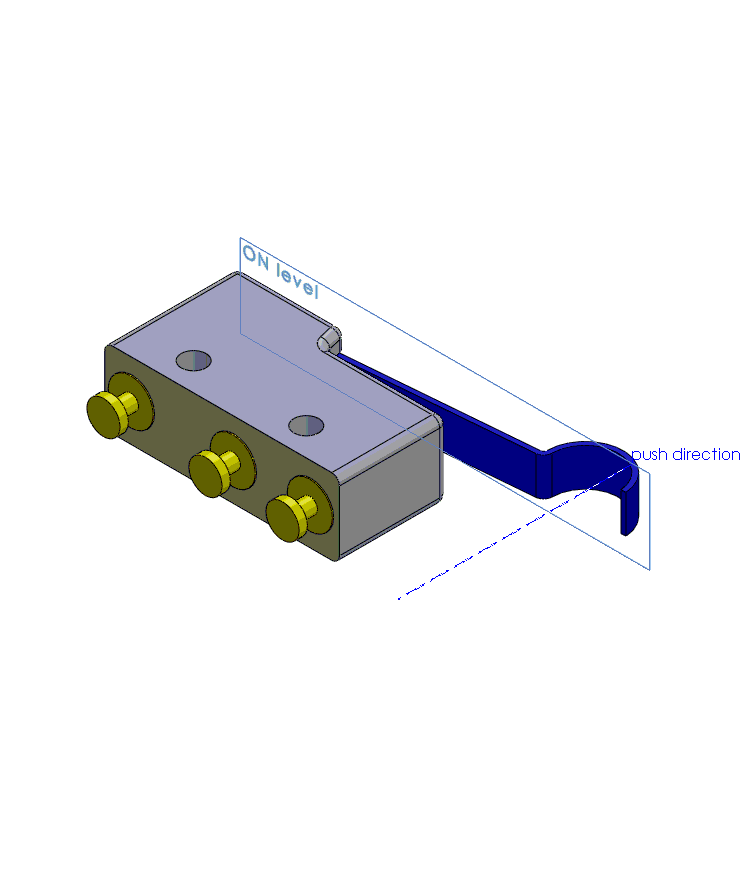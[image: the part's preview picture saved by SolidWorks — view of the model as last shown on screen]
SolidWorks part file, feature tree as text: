
SOLIDWORKS PART (.sldprt)
format: sldprt  version: not decoded by parser v0  size: 303,104 bytes
history: native  units: mm
features: sketch x5, fillet x3, cut_extrude x2, pattern_linear x2, plane x2, material x1, extrude x1, revolve x1 (+11 scaffold rows collapsed)
feature tree (28):
  scaffold x11  (default folders/planes/origin — collapsed)
  material  "Material <not specified>"
  sketch  "Sketch2"  dims[c1.D1=11.2mm c1.D2=19.8mm c2.D1=11.2mm c2.D3=9.0mm c2.D4=9.5mm c2.D5=9.1mm]
  extrude  "Boss-Extrude1"  Depth=6.4mm
  sketch  "Sketch3"  dims[D1=2.1mm D5=2.1mm D2=9.5mm D3=5.15mm D4=5.15mm D6=2.35mm D7=4.1mm D8=1.3mm]
  cut_extrude  "Cut-Extrude1"  Depth=16.4mm
  sketch  "Sketch4"  dims[c1.D1=3.2mm c1.D2=30.22mm c1.D3=~31.402716mm c1.D4=15.5mm c2.D1=3.2mm c2.D5=0.4mm c2.D6=1.0mm c2.D7=5.0mm]
  fillet  "Fillet1"  Radius=0.65mm
  sketch  "Sketch5"
  cut_extrude  "Cut-Extrude2"  Depth=16.4mm
  fillet  "Fillet2"  Radius=0.3mm
  fillet  "Fillet3"  Radius=0.7mm
  sketch  "Sketch6"  dims[D1=1.4mm D2=0.65mm D3=2.4mm D4=0.7mm D5=2.3mm D6=1.9mm D7=0.1mm]
  revolve  "Revolve1"  Angle=360deg
  pattern_linear  "LPattern1"  Count1=2 Count2=1 Spacing1=15.1mm Spacing2=10mm
  pattern_linear  "LPattern2"  Count1=2 Count2=1 Spacing1=8.6mm Spacing2=10mm
  plane  "ON level"  Offset=13mm
  plane  "Plane2"  Offset=28mm
decode coverage: 13 of 14 modeling features carry decoded parameters
note: ~ marks probable driven/reference dimensions
note: suppression state not decoded; provenance and decode notes live in map.json
